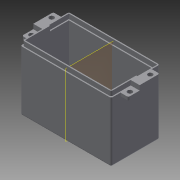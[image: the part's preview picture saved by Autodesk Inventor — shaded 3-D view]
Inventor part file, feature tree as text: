
AUTODESK INVENTOR PART (.ipt)
format: ipt  version: 2015 (Build 190159000, 159)  size: 262,656 bytes
history: native  units: mm
features: extrude x11, sketch x11, fillet x5, mirror x3, plane x1
ambient origin geometry x8: Origin, YZ Plane, XZ Plane, XY Plane, X Axis, Y Axis, Z Axis, Center Point
bodies: Solid1 (feature_tree)
feature tree (31):
  extrude  "Extrusion1"  Depth=55.0mm
  extrude  "Extrusion2"  Depth=58.0mm
  extrude  "Extrusion3"  Depth=1.5mm
  sketch  "Sketch7"  dims[d9=55.0mm d11=58.0mm d12=1.5mm d14=1.5mm d15=0.0mm d16=28.0mm d17=0.0mm]
  plane  "Work Plane1"
  extrude  "Extrusion4"  Depth=28.0mm TaperAngle=0.0deg
  mirror  "Mirror1"
  extrude  "Extrusion5"  Depth=15.0mm
  extrude  "Extrusion6"  Depth=13.375mm
  extrude  "Extrusion7"  Depth=2.0mm TaperAngle=0.0deg
  fillet  "Fillet1"  Radius=0.75mm
  extrude  "Extrusion8"  Depth=17.0mm
  fillet  "Fillet2"  Radius=3.0mm
  fillet  "Fillet3"  Radius=0.75mm
  extrude  "Extrusion10"  Depth=3.0mm TaperAngle=0.0deg
  mirror  "Mirror3"
  fillet  "Fillet7"  Radius=4.5mm
  fillet  "Fillet8"  Radius=14.0mm
  extrude  "Extrusion11"  Depth=3.3mm
  extrude  "Extrusion12"  Depth=1.0mm
  mirror  "Mirror4"
  sketch  "Sketch3"  dims[d0=35.25mm d1=55.0mm]
  sketch  "Sketch5"  dims[d4=38.25mm d5=58.0mm]
  sketch  "Sketch6"  dims[d6=1.5mm d7=1.5mm]
  sketch  "Sketch8"  dims[d18=1.5mm d19=0.0mm d20=15.0mm]
  sketch  "Sketch9"  dims[d21=1.0mm d22=13.375mm]
  sketch  "Sketch10"  dims[d23=8.375mm d24=27.5mm d25=2.0mm d26=0.0mm d27=0.75mm]
  sketch  "Sketch11"  dims[d29=56.5mm d31=17.0mm d32=3.0mm d33=0.0mm d34=0.75mm]
  sketch  "Sketch15"  dims[d36=56.5mm d38=3.0mm d39=0.0mm d40=4.5mm d41=14.0mm]
  sketch  "Sketch16"  dims[d42=20.5mm d43=3.3mm]
  sketch  "Sketch17"  dims[d44=5.0mm d45=0.0mm d46=1.0mm d47=9.9mm d48=7.5mm d49=27.5mm d50=5.0mm d51=0.0mm d52=1.0mm d53=1.0mm d65=0.75mm d66=17.0mm d69=16.75mm d70=16.75mm d78=5.0mm d79=12.75mm d80=2.0mm d81=7.25mm d82=5.0mm d83=0.0mm d84=17.0mm d85=1.0mm d86=1.0mm d87=3.0mm d88=2.5mm d89=3.5mm d90=5.0mm d91=0.0mm d92=3.0mm d93=3.5mm d94=2.5mm d95=2.0mm d96=0.0mm d97=28.75mm d98=11.5mm d99=20.0mm d100=12.75mm d101=5.0mm d64=1.0mm]
